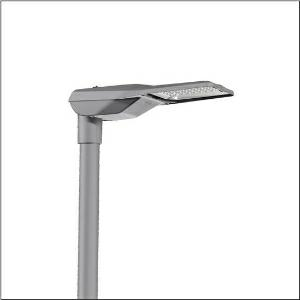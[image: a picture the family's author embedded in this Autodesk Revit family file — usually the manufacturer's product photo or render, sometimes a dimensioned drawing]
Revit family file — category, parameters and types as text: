
# Revit family: streetlight_sl_21_mini___st0_8a_5xe2c43s08jb_ad40
name_source: partatom
category: Lighting Fixtures
units: mm (PartAtom-declared; Revit-internal decimal feet)

## family parameters
Cut with Voids When Loaded = No
Host = Face
Light Source = No
Part Type = Normal
Room Calculation Point = No
Round Connector Dimension = Use Diameter
Shared = No

## types (1)
- --- (1 x LED, 13500 lm, 88.6 W, 4000K)
    Apparent Load = 89 VA
    CIE Flux Codes = 41 75 97 100 100
    Color Rendering = 70
    Color Temperature = 4000K
    Default Elevation = 1800 mm
    Description = Streetlight SL 21 mini, mast luminaire, primary light control with lens, of PMMA, primary optical cover: cover, of toughened safety glass, transparent, light distribution: ST0.8a, light emission: direct distribution, primary light characteristic: asymmetric, installation type: side-entry, post-top, LED, High Power LED, rated luminous flux: 13.500lm, luminous efficacy: 152lm/W, light colour: 740, colour temperature: 4000K, control gear: D4i, control: overheat protection, constant luminous flux control, time-dependent luminous flux control, flexible luminous flux parameterisation, pre-setting: logarithmic dimming characteristic, mains connection: 220..240V, AC, 50/60Hz, start of lifetime: 89W, end of service life: 92W, reduction: 41W, luminaire housing, of diecast aluminium, powder-coated, Siteco® metallic grey (DB 702S), corrosivity category C5 mid according to DIN EN ISO 12944, please order mast flange separately, inclination adjustable: 0°, 5°, 10°, 15°, sealing non-destructively replaceable, multi-level sealing system, length: 628mm, width: 235mm, height: 110mm, mast flange for spigot size: 42mm (side-entry): 5XC10008XM4, 60/48mm (side-entry/post-top): 5XC10108XM2, 76/60mm (side-entry/post-top): 5XC10108XM1, mounting height: 4..8m, Smart Interface above, protection rating (complete): IP66, insulation class (complete): insulation class II (safety insulation), certification: CE, ENEC, ENEC+, VDE, impact resistance: IK10, permissible operating ambient temperature for outdoor applications: -40..+50°C, standard-compliant lighting for roads and squares, packaging unit: 1 piece

Light Distribution: ST0.8a
    Height = 110 mm
    Lamp = 1 x LED
    Lamp Light Flux = 13500 lm
    Lamp Power = 88.6 W
    Lamp count = 1
    Length = 625 mm
    Luminous efficacy = 152 lm/W
    Manufacturer = Siteco
    ModVariant = No
    Model = 5XE2C43S08JB
    Number of Poles = 1
    OnlyDefault = Yes
    Power Factor = 1
    Product Name = Streetlight SL 21 mini | ST0.8a
    Product group = mast luminaire | pylon top
    ProductGroupID = 6100
    Protection Class = Protection class II
    Protection Degree = IP 66
    RLX_Detail_Level = 1
    RLX_Emergency_Light_Flux = 0 lm
    RLX_Emergency_Type = 0
    RLX_Emergency_Type_DB = No
    RlxData = <blob elided: 26185 chars, md5=2df7c29c>
    Socket = socket
    Standby Power = 0 W
    System Light Flux = 13500 lm
    System Power = 89 W
    Type Comments = factory setting: luminous flux: 100 % | dim-lin: 254 | 915 mA
    Type Image = l_1003515.jpg
    URL = http://relux.com
    VarID = @adj_011225
    Voltage = 0 V
    Weight = 0.00 kg
    Width = 234 mm

## geometry (parser evidence)
native form markers: Blend x4, Sweep x10
no freeform markers — native parametric forms only
